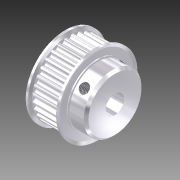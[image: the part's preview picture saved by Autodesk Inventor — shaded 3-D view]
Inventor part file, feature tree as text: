
AUTODESK INVENTOR PART (.ipt)
format: ipt  version: 2011 (Build 150239000, 239)  size: 694,784 bytes
history: native  units: mm
features: thread x2, imported_body x1
ambient origin geometry x8: Origin, YZ Plane, XZ Plane, XY Plane, X Axis, Y Axis, Z Axis, Center Point
bodies: Solid1 (feature_tree)
feature tree (3):
  imported_body  "Base1"
  thread  "Thread1"  [1 undecoded]
  thread  "Thread2"  [1 undecoded]
note: 2 required parameter values undecoded (feature->parameter linkage not recoverable at this tier; creation-order binding heuristic only, values carry confidence <= 0.55)
